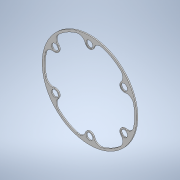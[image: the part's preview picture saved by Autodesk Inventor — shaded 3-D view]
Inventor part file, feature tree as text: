
AUTODESK INVENTOR PART (.ipt)
format: ipt  version: 2020 (Build 240168000, 168)  size: 177,664 bytes
history: native  units: in
note: dims shown in document units (in); Inventor stores cm internally (conversion verified against a paired STEP export)
features: extrude x1, sketch x1
ambient origin geometry x8: Origin, YZ Plane, XZ Plane, XY Plane, X Axis, Y Axis, Z Axis, Center Point
bodies: Solid1 (feature_tree)
feature tree (2):
  extrude  "Extrusion1"  Depth=0.0591in
  sketch  "Sketch1"  dims[d0=5.3543in d1=5.1181in d2=120.0deg d3=120.0deg d4=120.0deg d5=120.0deg d6=0.378in d7=2.2638in d8=2.3622in d10=360.0deg d12=0.0591in d13=2.3622in d15=360.0deg d17=0.7874in d18=0.7874in d19=2.3622in d21=360.0deg d23=0.0591in d24=0.0in]
